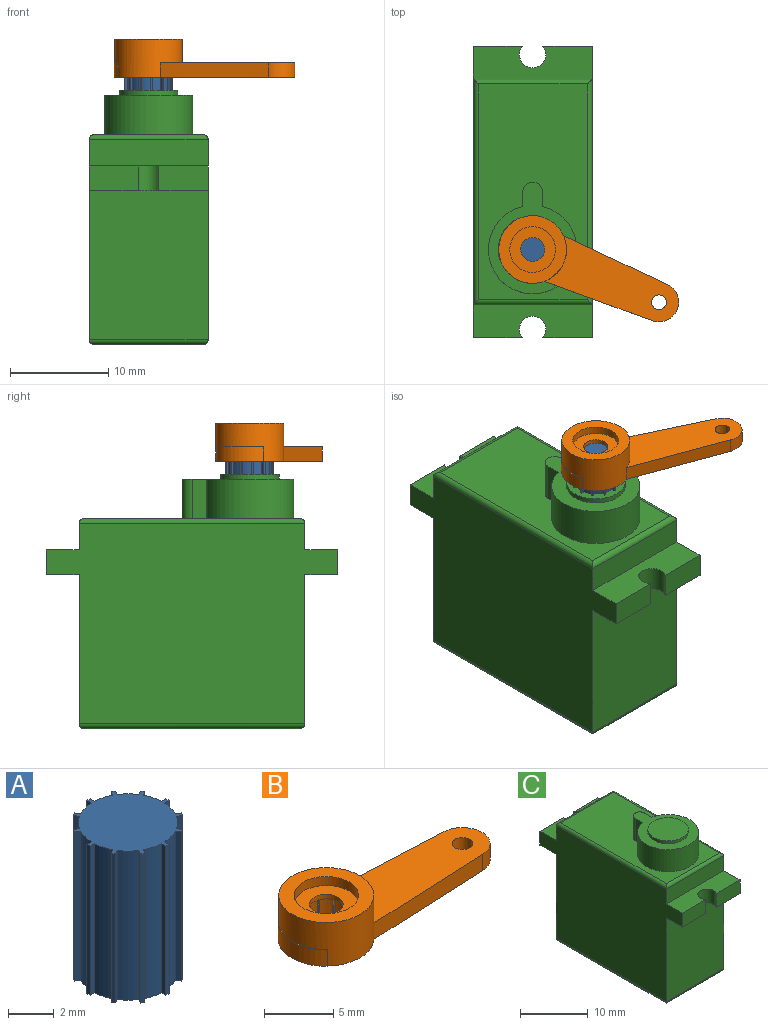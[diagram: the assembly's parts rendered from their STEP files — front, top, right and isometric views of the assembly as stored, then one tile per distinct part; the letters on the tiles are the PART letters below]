
ASSEMBLY  parts=3 mates=2
PART A: 50 faces, bbox 4.9x4.9x8 mm
  f0: cylinder r=2.45mm len=8mm, axis (0,0,-1), area 1.6mm2, adj f1,f2,f3,f4
  f1: plane 8x0.28mm, normal (-1,0,0), area 2.2mm2, adj f0,f3,f4,f5
  f2: plane 8x0.28mm, normal (1,0,0), area 2.2mm2, adj f0,f3,f4,f49
  f3: plane 4.9x4.9mm, normal (0,0,1), area 15.5mm2, adj f0,f1,f2,f5,f6,f7,f8,f9
  f4: plane 4.9x4.9mm, normal (0,0,-1), area 15.5mm2, adj f0,f1,f2,f5,f6,f7,f8,f9
  f5: cylinder r=2.17mm len=8mm, axis (0,0,-1), area 7.5mm2, adj f1,f3,f4,f8
  f6: cylinder r=2.45mm len=8mm, axis (0,0,-1), area 1.6mm2, adj f3,f4,f7,f8
  f7: plane 8x0.24mm, normal (-0.87,-0.5,0), area 2.2mm2, adj f3,f4,f6,f9
  f8: plane 8x0.24mm, normal (0.87,0.5,0), area 2.2mm2, adj f3,f4,f5,f6
  f9: cylinder r=2.17mm len=8mm, axis (0,0,-1), area 7.5mm2, adj f3,f4,f7,f12
  f10: cylinder r=2.45mm len=8mm, axis (0,0,-1), area 1.6mm2, adj f3,f4,f11,f12
  f11: plane 8x0.24mm, normal (-0.5,-0.87,0), area 2.2mm2, adj f3,f4,f10,f13
  f12: plane 8x0.24mm, normal (0.5,0.87,0), area 2.2mm2, adj f3,f4,f9,f10
  f13: cylinder r=2.17mm len=8mm, axis (0,0,-1), area 7.5mm2, adj f3,f4,f11,f16
  f14: cylinder r=2.45mm len=8mm, axis (0,0,-1), area 1.6mm2, adj f3,f4,f15,f16
  f15: plane 8x0.28mm, normal (0,-1,0), area 2.2mm2, adj f3,f4,f14,f17
  f16: plane 8x0.28mm, normal (0,1,0), area 2.2mm2, adj f3,f4,f13,f14
  f17: cylinder r=2.17mm len=8mm, axis (0,0,-1), area 7.5mm2, adj f3,f4,f15,f20
  f18: cylinder r=2.45mm len=8mm, axis (0,0,-1), area 1.6mm2, adj f3,f4,f19,f20
  f19: plane 8x0.24mm, normal (0.5,-0.87,0), area 2.2mm2, adj f3,f4,f18,f21
  f20: plane 8x0.24mm, normal (-0.5,0.87,0), area 2.2mm2, adj f3,f4,f17,f18
  f21: cylinder r=2.17mm len=8mm, axis (0,0,-1), area 7.5mm2, adj f3,f4,f19,f24
  f22: cylinder r=2.45mm len=8mm, axis (0,0,-1), area 1.6mm2, adj f3,f4,f23,f24
  f23: plane 8x0.24mm, normal (0.87,-0.5,0), area 2.2mm2, adj f3,f4,f22,f25
  f24: plane 8x0.24mm, normal (-0.87,0.5,0), area 2.2mm2, adj f3,f4,f21,f22
  f25: cylinder r=2.17mm len=8mm, axis (0,0,-1), area 7.5mm2, adj f3,f4,f23,f28
  f26: cylinder r=2.45mm len=8mm, axis (0,0,-1), area 1.6mm2, adj f3,f4,f27,f28
  f27: plane 8x0.28mm, normal (1,0,0), area 2.2mm2, adj f3,f4,f26,f29
  f28: plane 8x0.28mm, normal (-1,0,0), area 2.2mm2, adj f3,f4,f25,f26
  f29: cylinder r=2.17mm len=8mm, axis (0,0,-1), area 7.5mm2, adj f3,f4,f27,f32
  f30: cylinder r=2.45mm len=8mm, axis (0,0,-1), area 1.6mm2, adj f3,f4,f31,f32
  f31: plane 8x0.24mm, normal (0.87,0.5,0), area 2.2mm2, adj f3,f4,f30,f33
  f32: plane 8x0.24mm, normal (-0.87,-0.5,0), area 2.2mm2, adj f3,f4,f29,f30
  f33: cylinder r=2.17mm len=8mm, axis (0,0,-1), area 7.5mm2, adj f3,f4,f31,f36
  f34: cylinder r=2.45mm len=8mm, axis (0,0,-1), area 1.6mm2, adj f3,f4,f35,f36
  f35: plane 8x0.24mm, normal (0.5,0.87,0), area 2.2mm2, adj f3,f4,f34,f37
  f36: plane 8x0.24mm, normal (-0.5,-0.87,0), area 2.2mm2, adj f3,f4,f33,f34
  f37: cylinder r=2.17mm len=8mm, axis (0,0,-1), area 7.5mm2, adj f3,f4,f35,f40
  f38: cylinder r=2.45mm len=8mm, axis (0,0,-1), area 1.6mm2, adj f3,f4,f39,f40
  f39: plane 8x0.28mm, normal (0,1,0), area 2.2mm2, adj f3,f4,f38,f41
  f40: plane 8x0.28mm, normal (0,-1,0), area 2.2mm2, adj f3,f4,f37,f38
  f41: cylinder r=2.17mm len=8mm, axis (0,0,-1), area 7.5mm2, adj f3,f4,f39,f44
  f42: cylinder r=2.45mm len=8mm, axis (0,0,-1), area 1.6mm2, adj f3,f4,f43,f44
  f43: plane 8x0.24mm, normal (-0.5,0.87,0), area 2.2mm2, adj f3,f4,f42,f45
  f44: plane 8x0.24mm, normal (0.5,-0.87,0), area 2.2mm2, adj f3,f4,f41,f42
  f45: cylinder r=2.17mm len=8mm, axis (0,0,-1), area 7.5mm2, adj f3,f4,f43,f48
  f46: cylinder r=2.45mm len=8mm, axis (0,0,-1), area 1.6mm2, adj f3,f4,f47,f48
  f47: plane 8x0.24mm, normal (-0.87,0.5,0), area 2.2mm2, adj f3,f4,f46,f49
  f48: plane 8x0.24mm, normal (0.87,-0.5,0), area 2.2mm2, adj f3,f4,f45,f46
  f49: cylinder r=2.17mm len=8mm, axis (0,0,-1), area 7.5mm2, adj f2,f3,f4,f47
PART B: 64 faces, bbox 19.5x6.9x3.9 mm
  f0: cylinder r=2.45mm len=2.65mm, axis (0,0,-1), area 0.5mm2, adj f1,f47,f56,f58
  f1: plane 2.65x0.28mm, normal (-1,0,0), area 0.7mm2, adj f0,f2,f56,f58
  f2: cylinder r=2.17mm len=2.65mm, axis (0,0,-1), area 2.5mm2, adj f1,f3,f56,f58
  f3: plane 2.65x0.24mm, normal (0.87,-0.5,0), area 0.7mm2, adj f2,f4,f56,f58
  f4: cylinder r=2.45mm len=2.65mm, axis (0,0,-1), area 0.5mm2, adj f3,f5,f56,f58
  f5: plane 2.65x0.24mm, normal (-0.87,0.5,0), area 0.7mm2, adj f4,f6,f56,f58
  f6: cylinder r=2.17mm len=2.65mm, axis (0,0,-1), area 2.5mm2, adj f5,f7,f56,f58
  f7: plane 2.65x0.24mm, normal (0.5,-0.87,0), area 0.7mm2, adj f6,f8,f56,f58
  f8: cylinder r=2.45mm len=2.65mm, axis (0,0,-1), area 0.5mm2, adj f7,f9,f56,f58
  f9: plane 2.65x0.24mm, normal (-0.5,0.87,0), area 0.7mm2, adj f8,f10,f56,f58
  f10: cylinder r=2.17mm len=2.65mm, axis (0,0,-1), area 2.5mm2, adj f9,f11,f56,f58
  f11: plane 2.65x0.28mm, normal (0,-1,0), area 0.7mm2, adj f10,f12,f56,f58
  f12: cylinder r=2.45mm len=2.65mm, axis (0,0,-1), area 0.5mm2, adj f11,f13,f56,f58
  f13: plane 2.65x0.28mm, normal (0,1,0), area 0.7mm2, adj f12,f14,f56,f58
  f14: cylinder r=2.17mm len=2.65mm, axis (0,0,-1), area 2.5mm2, adj f13,f15,f56,f58
  f15: plane 2.65x0.24mm, normal (-0.5,-0.87,0), area 0.7mm2, adj f14,f16,f56,f58
  f16: cylinder r=2.45mm len=2.65mm, axis (0,0,-1), area 0.5mm2, adj f15,f17,f56,f58
  f17: plane 2.65x0.24mm, normal (0.5,0.87,0), area 0.7mm2, adj f16,f18,f56,f58
  f18: cylinder r=2.17mm len=2.65mm, axis (0,0,-1), area 2.5mm2, adj f17,f19,f56,f58
  f19: plane 2.65x0.24mm, normal (-0.87,-0.5,0), area 0.7mm2, adj f18,f20,f56,f58
  f20: cylinder r=2.45mm len=2.65mm, axis (0,0,-1), area 0.5mm2, adj f19,f21,f56,f58
  f21: plane 2.65x0.24mm, normal (0.87,0.5,0), area 0.7mm2, adj f20,f22,f56,f58
  f22: cylinder r=2.17mm len=2.65mm, axis (0,0,-1), area 2.5mm2, adj f21,f23,f56,f58
  f23: plane 2.65x0.28mm, normal (-1,0,0), area 0.7mm2, adj f22,f24,f56,f58
  f24: cylinder r=2.45mm len=2.65mm, axis (0,0,-1), area 0.5mm2, adj f23,f25,f56,f58
  f25: plane 2.65x0.28mm, normal (1,0,0), area 0.7mm2, adj f24,f26,f56,f58
  f26: cylinder r=2.17mm len=2.65mm, axis (0,0,-1), area 2.5mm2, adj f25,f27,f56,f58
  f27: plane 2.65x0.24mm, normal (-0.87,0.5,0), area 0.7mm2, adj f26,f28,f56,f58
  f28: cylinder r=2.45mm len=2.65mm, axis (0,0,-1), area 0.5mm2, adj f27,f29,f56,f58
  f29: plane 2.65x0.24mm, normal (0.87,-0.5,0), area 0.7mm2, adj f28,f30,f56,f58
  f30: cylinder r=2.17mm len=2.65mm, axis (0,0,-1), area 2.5mm2, adj f29,f31,f56,f58
  f31: plane 2.65x0.24mm, normal (-0.5,0.87,0), area 0.7mm2, adj f30,f32,f56,f58
  f32: cylinder r=2.45mm len=2.65mm, axis (0,0,-1), area 0.5mm2, adj f31,f33,f56,f58
  f33: plane 2.65x0.24mm, normal (0.5,-0.87,0), area 0.7mm2, adj f32,f34,f56,f58
  f34: cylinder r=2.17mm len=2.65mm, axis (0,0,-1), area 2.5mm2, adj f33,f35,f56,f58
  f35: plane 2.65x0.28mm, normal (0,1,0), area 0.7mm2, adj f34,f36,f56,f58
  f36: cylinder r=2.45mm len=2.65mm, axis (0,0,-1), area 0.5mm2, adj f35,f37,f56,f58
  f37: plane 2.65x0.28mm, normal (0,-1,0), area 0.7mm2, adj f36,f38,f56,f58
  f38: cylinder r=2.17mm len=2.65mm, axis (0,0,-1), area 2.5mm2, adj f37,f39,f56,f58
  f39: plane 2.65x0.24mm, normal (0.5,0.87,0), area 0.7mm2, adj f38,f40,f56,f58
  f40: cylinder r=2.45mm len=2.65mm, axis (0,0,-1), area 0.5mm2, adj f39,f41,f56,f58
  f41: plane 2.65x0.24mm, normal (-0.5,-0.87,0), area 0.7mm2, adj f40,f42,f56,f58
  f42: cylinder r=2.17mm len=2.65mm, axis (0,0,-1), area 2.5mm2, adj f41,f43,f56,f58
  f43: plane 2.65x0.24mm, normal (0.87,0.5,0), area 0.7mm2, adj f42,f44,f56,f58
  f44: cylinder r=2.45mm len=2.65mm, axis (0,0,-1), area 0.5mm2, adj f43,f45,f56,f58
  f45: plane 2.65x0.24mm, normal (-0.87,-0.5,0), area 0.7mm2, adj f44,f46,f56,f58
  f46: cylinder r=2.17mm len=2.65mm, axis (0,0,-1), area 2.5mm2, adj f45,f47,f56,f58
  f47: plane 2.65x0.28mm, normal (1,0,0), area 0.7mm2, adj f0,f46,f56,f58
  f48: plane 5.04x1.14mm, normal (0,0,1), area 0.3mm2, adj f49,f50,f54,f62
  f49: plane 1.45x0.08mm, normal (-0.04,-1,0), area 0.1mm2, adj f48,f50,f56,f62
  f50: cylinder r=3.45mm len=6.9mm, axis (0,0,-1), area 67.1mm2, adj f48,f49,f51,f53,f54,f55,f56,f57
  f51: plane 11.68x1.45mm, normal (0.04,-1,0), area 17mm2, adj f50,f52,f55,f56
  f52: cylinder r=2mm len=4mm, axis (0,0,-1), area 8.9mm2, adj f51,f53,f55,f56
  f53: plane 11.68x1.45mm, normal (0.04,1,0), area 17mm2, adj f50,f52,f55,f56
  f54: plane 1.45x0.07mm, normal (-0.04,1,0), area 0.1mm2, adj f48,f50,f56,f62
  f55: plane 13.59x5.04mm, normal (0,0,1), area 53.1mm2, adj f50,f51,f52,f53,f63
  f56: plane 19.45x6.9mm, normal (0,0,-1), area 75.3mm2, adj f0,f1,f2,f3,f4,f5,f6,f7
  f57: plane 6.9x6.9mm, normal (0,0,1), area 20.3mm2, adj f50,f59
  f58: plane 4.9x4.9mm, normal (0,0,-1), area 10.8mm2, adj f0,f1,f2,f3,f4,f5,f6,f7
  f59: cylinder r=2.33mm len=4.66mm, axis (0,0,1), area 11.7mm2, adj f57,f60
  f60: plane 4.66x4.66mm, normal (0,0,1), area 12.4mm2, adj f59,f61
  f61: cylinder r=1.22mm len=2.44mm, axis (0,0,1), area 3.1mm2, adj f58,f60
  f62: cylinder r=3.5mm len=5.03mm, axis (0,0,-1), area 8.1mm2, adj f48,f49,f54,f56
  f63: cylinder r=0.75mm len=1.5mm, axis (0,0,1), area 6.8mm2, adj f55,f56
PART C: 33 faces, bbox 12.1x29.7x25.9 mm
  f0: plane 12.1x2.7mm, normal (0,1,0), area 32.7mm2, adj f4,f6,f16,f29
  f1: plane 12.1x2.7mm, normal (0,-1,0), area 32.7mm2, adj f4,f6,f17,f24
  f2: plane 22x11.1mm, normal (0,0,1), area 176.2mm2, adj f8,f9,f10,f11,f15,f16,f17,f18
  f3: plane 15.2x12.1mm, normal (0,1,0), area 183.9mm2, adj f4,f6,f20,f30
  f4: plane 29.69x20.4mm, normal (-1,0,0), area 485.9mm2, adj f0,f1,f3,f5,f15,f19,f24,f25
  f5: plane 15.2x12.1mm, normal (0,-1,0), area 183.9mm2, adj f4,f6,f21,f25
  f6: plane 29.69x20.4mm, normal (1,0,0), area 485.9mm2, adj f0,f1,f3,f5,f18,f22,f23,f24
  f7: plane 22x11.1mm, normal (0,0,-1), area 244.2mm2, adj f19,f20,f21,f22
  f8: plane 4x1.5mm, normal (1,0,0), area 6mm2, adj f2,f9,f11,f12
  f9: cylinder r=1mm len=4mm, axis (0,0,-1), area 12.6mm2, adj f2,f8,f10,f12
  f10: plane 4x1.5mm, normal (-1,0,0), area 6mm2, adj f2,f9,f11,f12
  f11: cylinder r=4.5mm len=9mm, axis (0,0,-1), area 105mm2, adj f2,f8,f10,f12
  f12: plane 11.39x9mm, normal (0,0,1), area 39.9mm2, adj f8,f9,f10,f11,f13
  f13: cylinder r=2.99mm len=5.98mm, axis (0,0,-1), area 9.4mm2, adj f12,f14
  f14: plane 5.98x5.98mm, normal (0,0,1), area 28.1mm2, adj f13
  f15: cylinder r=0.5mm len=23mm, axis (0,1,0), area 17.8mm2, adj f2,f4,f16,f17
  f16: cylinder r=0.5mm len=12.1mm, axis (1,0,0), area 9.2mm2, adj f0,f2,f15,f18
  f17: cylinder r=0.5mm len=12.1mm, axis (-1,0,0), area 9.2mm2, adj f1,f2,f15,f18
  f18: cylinder r=0.5mm len=23mm, axis (0,-1,0), area 17.8mm2, adj f2,f6,f16,f17
  f19: cylinder r=0.5mm len=23mm, axis (0,-1,0), area 17.8mm2, adj f4,f7,f20,f21
  f20: cylinder r=0.5mm len=12.1mm, axis (-1,0,0), area 9.2mm2, adj f3,f7,f19,f22
  f21: cylinder r=0.5mm len=12.1mm, axis (1,0,0), area 9.2mm2, adj f5,f7,f19,f22
  f22: cylinder r=0.5mm len=23mm, axis (0,1,0), area 17.8mm2, adj f6,f7,f20,f21
  f23: plane 5.01x2.5mm, normal (0,-1,0), area 12.5mm2, adj f6,f24,f25,f27
  f24: plane 12.1x3.35mm, normal (0,0,1), area 35.5mm2, adj f1,f4,f6,f23,f26,f27
  f25: plane 12.1x3.35mm, normal (0,0,-1), area 35.5mm2, adj f4,f5,f6,f23,f26,f27
  f26: plane 4.98x2.5mm, normal (0,-1,0), area 12.5mm2, adj f4,f24,f25,f27
  f27: cylinder r=1.35mm len=2.7mm, axis (0,0,-1), area 15.2mm2, adj f23,f24,f25,f26
  f28: plane 5.01x2.5mm, normal (0,1,0), area 12.5mm2, adj f6,f29,f30,f32
  f29: plane 12.1x3.35mm, normal (0,0,1), area 35.5mm2, adj f0,f4,f6,f28,f31,f32
  f30: plane 12.1x3.35mm, normal (0,0,-1), area 35.5mm2, adj f3,f4,f6,f28,f31,f32
  f31: plane 4.98x2.5mm, normal (0,1,0), area 12.5mm2, adj f4,f29,f30,f32
  f32: cylinder r=1.35mm len=2.7mm, axis (0,0,-1), area 15.2mm2, adj f28,f29,f30,f31
PLACE A rot(axis=(0,0,-1),22.6deg) t=(-0.77,0.98,0.56)mm
PLACE B rot(axis=(0,0,-1),22.6deg) t=(-0.77,0.98,-2.09)mm
PLACE C t=(-3.03,1.43,0.06)mm fixed
MATE revolute A.f0 <-> C.f11  axis (0,0,-1) through (-3.03,-4.46,15.26)mm
MATE fastened A.f0 <-> B.f0  axis (0,0,1) through (-3.03,-4.46,19.26)mm
